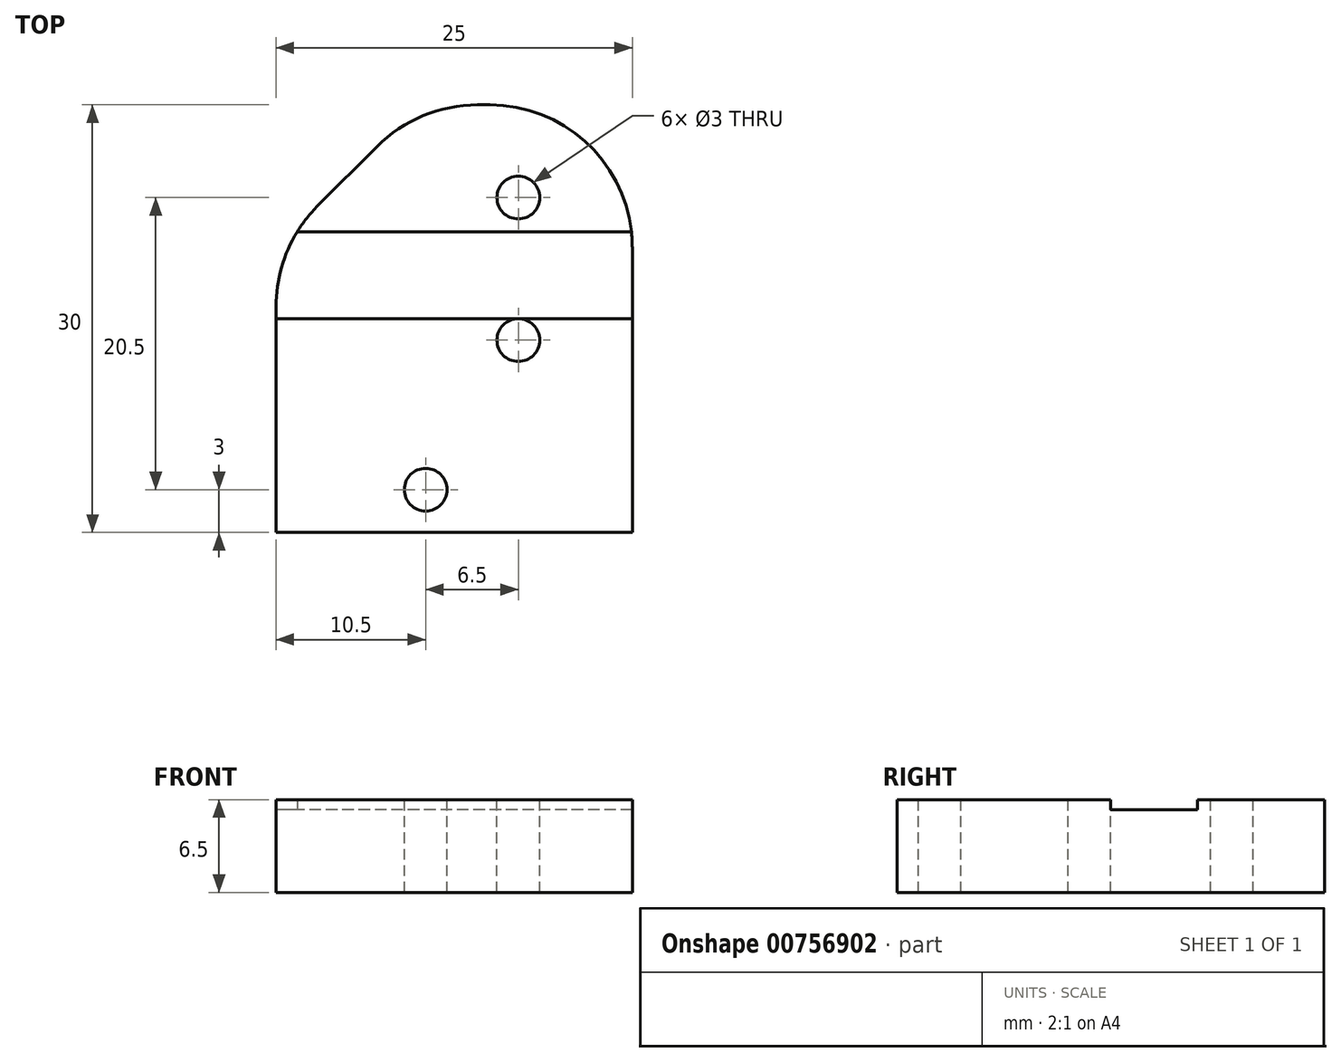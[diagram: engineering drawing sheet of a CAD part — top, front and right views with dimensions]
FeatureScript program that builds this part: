
annotation { "Feature Type Name" : "Feature", "Feature Type Description" : "" }
export const myFeature = defineFeature(function(context is Context, id is Id, definition is map)
    precondition{}
    {
        {
            var Q0;
            Q0=qCreatedBy(makeId("Top.planeOp"),FACE);
            var sketch = newSketch(context, id + "F0", { "sketchPlane" : qUnion([Q0])});
            skLineSegment(sketch, "E0.bottom", {"start": v(12.5, -15) * mm, "end": v(-12.5, -15) * mm});
            skLineSegment(sketch, "E0.top", {"start": v(12.5, 15) * mm, "end": v(-12.5, 15) * mm});
            skLineSegment(sketch, "E0.left", {"start": v(12.5, -15) * mm, "end": v(12.5, 15) * mm});
            skLineSegment(sketch, "E0.right", {"start": v(-12.5, -15) * mm, "end": v(-12.5, 15) * mm});
            skPoint(sketch, "E0.middle", {"position": v(0, 0) * mm});
            skSolve(sketch);
        }
        {
            var Q0;
            Q0=makeQuery(id+"F0.imprint","IMPRINT",FACE,{"disambiguationData":[TD([[makeQuery(id+"F0.imprint","IMPRINT",EDGE,{"derivedFrom":sQuery(id+"F0.wireOp",EDGE,"E0.bottom")}),-1.0]])]});
            extrude(context, id + "F1", {"entities" : qUnion([Q0]), "depth" : 6.5 * mm, "offsetDistance" : 25 * mm});
        }
        {
            var Q0;
            Q0=makeQuery(id+"F1.opExtrude","CAP_FACE",FACE,{"disambiguationData":[OSD([sQuery(id+"F0.wireOp",EDGE,"E0.bottom"),sQuery(id+"F0.wireOp",EDGE,"E0.top"),sQuery(id+"F0.wireOp",EDGE,"E0.left"),sQuery(id+"F0.wireOp",EDGE,"E0.right")])],"isStart":false});
            var sketch = newSketch(context, id + "F2", { "sketchPlane" : qUnion([Q0])});
            skCircle(sketch, "E1", {"center": v(-2, -12) * mm, "radius": 1.5 * mm});
            skPoint(sketch, "E1.centerSnap0", {"position": v(0, -15) * mm});
            skCircle(sketch, "E2", {"center": v(4.5, -1.5) * mm, "radius": 1.5 * mm});
            skCircle(sketch, "E3", {"center": v(4.5, 8.5) * mm, "radius": 1.5 * mm});
            skSolve(sketch);
        }
        {
            var Q0;
            Q0=qSketchRegion(id+"F2",true);
            extrude(context, id + "F3", {"entities" : qUnion([Q0]), "operationType" : NewBodyOperationType.REMOVE, "endBound" : BoundingType.THROUGH_ALL, "oppositeDirection" : true, "depth" : 25 * mm, "offsetDistance" : 25 * mm});
        }
        {
            var Q0;
            Q0=makeQuery(id+"F1.opExtrude","CAP_FACE",FACE,{"disambiguationData":[OSD([sQuery(id+"F0.wireOp",EDGE,"E0.bottom"),sQuery(id+"F0.wireOp",EDGE,"E0.top"),sQuery(id+"F0.wireOp",EDGE,"E0.left"),sQuery(id+"F0.wireOp",EDGE,"E0.right")])],"isStart":false});
            var sketch = newSketch(context, id + "F4", { "sketchPlane" : qUnion([Q0])});
            skLineSegment(sketch, "E4.bottom", {"start": v(12.5, 6.1) * mm, "end": v(-12.5, 6.1) * mm});
            skLineSegment(sketch, "E4.top", {"start": v(12.5, 0) * mm, "end": v(-12.5, 0) * mm});
            skLineSegment(sketch, "E4.left", {"start": v(12.5, 6.1) * mm, "end": v(12.5, 0) * mm});
            skLineSegment(sketch, "E4.right", {"start": v(-12.5, 6.1) * mm, "end": v(-12.5, 0) * mm});
            skSolve(sketch);
        }
        {
            var Q0;
            Q0 = qSketchRegion(id + "F4", true);
            extrude(context, id + "F5", {"entities" : qUnion([Q0]), "operationType" : NewBodyOperationType.REMOVE, "oppositeDirection" : true, "depth" : 0.7 * mm, "offsetDistance" : 25 * mm});
        }
        {
            var Q0;
            Q0=makeQuery(id+"F1.opExtrude","SWEPT_EDGE",EDGE,{"disambiguationData":[OSD([sQuery(id+"F0.wireOp",EDGE,"E0.top"),sQuery(id+"F0.wireOp",EDGE,"E0.right")])]});
            chamfer(context, id + "F6", {"entities" : qUnion([Q0]), "width" : 10 * mm, "tangentPropagation" : true});
        }
        {
            var Q0;
            {var subQ0=sQuery(id+"F0.wireOp",EDGE,"E0.top");Q0=makeQuery(id+"F6.opChamfer","BLEND_EDGE",EDGE,{"blendedFrom":[makeQuery(id+"F1.opExtrude","SWEPT_EDGE",EDGE,{"disambiguationData":[OSD([subQ0,sQuery(id+"F0.wireOp",EDGE,"E0.right")])]}),makeQuery(id+"F1.opExtrude","SWEPT_FACE",FACE,{"disambiguationData":[OSD([subQ0])]})],"blendedInto":[makeQuery(id+"F1.opExtrude","SWEPT_FACE",FACE,{"disambiguationData":[OSD([subQ0])]})]});}
            var Q1;
            {var subQ0=sQuery(id+"F0.wireOp",EDGE,"E0.right");Q1=makeQuery(id+"F6.opChamfer","BLEND_EDGE",EDGE,{"blendedFrom":[makeQuery(id+"F1.opExtrude","SWEPT_EDGE",EDGE,{"disambiguationData":[OSD([sQuery(id+"F0.wireOp",EDGE,"E0.top"),subQ0])]}),makeQuery(id+"F1.opExtrude","SWEPT_FACE",FACE,{"disambiguationData":[OSD([subQ0])]})],"blendedInto":[makeQuery(id+"F1.opExtrude","SWEPT_FACE",FACE,{"disambiguationData":[OSD([subQ0])]})]});}
            var Q2;
            Q2=makeQuery(id+"F1.opExtrude","SWEPT_EDGE",EDGE,{"disambiguationData":[OSD([sQuery(id+"F0.wireOp",EDGE,"E0.top"),sQuery(id+"F0.wireOp",EDGE,"E0.left")])]});
            fillet(context, id + "F7", {"entities" : qUnion([Q0, Q1, Q2]), "radius" : 10 * mm, "tangentPropagation" : true, "allowEdgeOverflow" : false});
        }
    });
